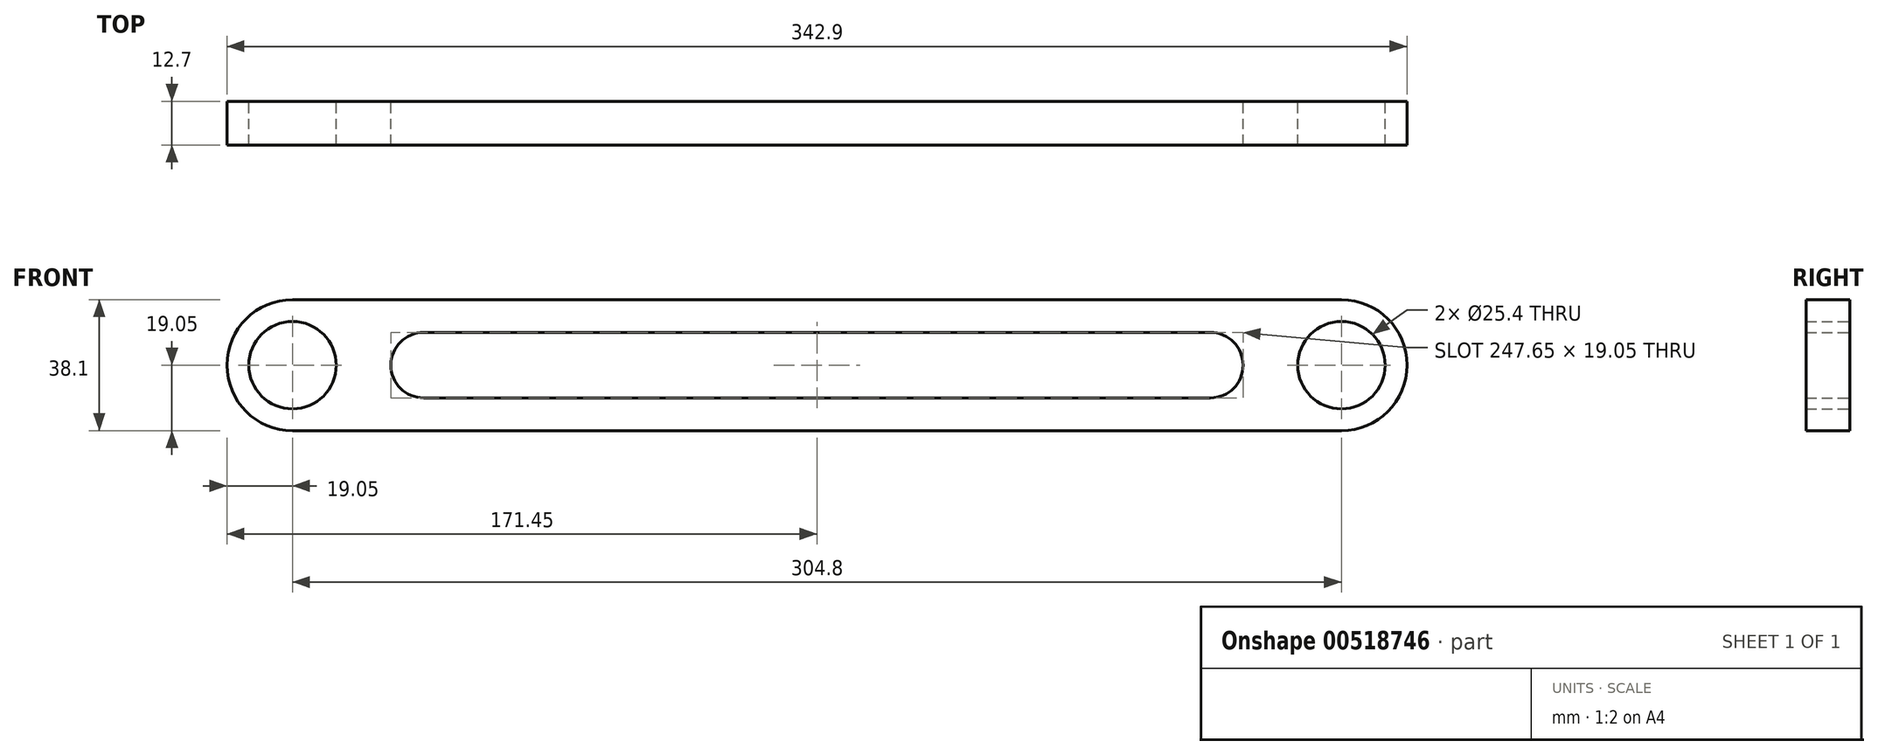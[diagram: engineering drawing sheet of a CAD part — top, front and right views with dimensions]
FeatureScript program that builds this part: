
annotation { "Feature Type Name" : "Feature", "Feature Type Description" : "" }
export const myFeature = defineFeature(function(context is Context, id is Id, definition is map)
    precondition{}
    {
        {
            var Q0;
            Q0=qCreatedBy(makeId("Front.planeOp"),FACE);
            var sketch = newSketch(context, id + "F0", { "sketchPlane" : qUnion([Q0])});
            skLineSegment(sketch, "E0.bottom", {"start": v(-152.4, 19.05) * mm, "end": v(152.4, 19.05) * mm});
            skLineSegment(sketch, "E0.top", {"start": v(-152.4, -19.05) * mm, "end": v(152.4, -19.05) * mm});
            skPoint(sketch, "E0.middle", {"position": v(0, 0) * mm});
            skArc(sketch, "E1", {"start": v(-152.4, 19.05) * mm, "mid": v(-171.45, 0) * mm, "end": v(-152.4, -19.05) * mm});
            skArc(sketch, "E2", {"start": v(152.4, -19.05) * mm, "mid": v(171.45, 0) * mm, "end": v(152.4, 19.05) * mm});
            skCircle(sketch, "E3", {"center": v(-152.4, 0) * mm, "radius": 12.7 * mm});
            skCircle(sketch, "E4", {"center": v(152.4, 0) * mm, "radius": 12.7 * mm});
            skLineSegment(sketch, "E5.bottom", {"start": v(-114.3, 9.53) * mm, "end": v(114.3, 9.53) * mm});
            skLineSegment(sketch, "E5.top", {"start": v(-114.3, -9.53) * mm, "end": v(114.3, -9.53) * mm});
            skArc(sketch, "E6", {"start": v(-114.3, 9.53) * mm, "mid": v(-123.83, 0) * mm, "end": v(-114.3, -9.53) * mm});
            skArc(sketch, "E7", {"start": v(114.3, 9.53) * mm, "mid": v(123.83, 0) * mm, "end": v(114.3, -9.53) * mm});
            skSolve(sketch);
        }
        {
            var Q0;
            Q0=makeQuery(id+"F0.imprint","IMPRINT",FACE,{"disambiguationData":[TD([[makeQuery(id+"F0.imprint","IMPRINT",EDGE,{"derivedFrom":sQuery(id+"F0.wireOp",EDGE,"E0.bottom")}),-1.0]])]});
            extrude(context, id + "F1", {"entities" : qUnion([Q0]), "depth" : 12.7 * mm, "offsetDistance" : 25.4 * mm});
        }
    });
